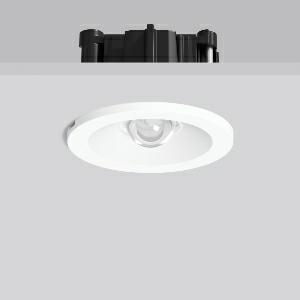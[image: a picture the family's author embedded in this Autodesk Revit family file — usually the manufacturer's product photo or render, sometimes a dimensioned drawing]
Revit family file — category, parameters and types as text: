
# Revit family: turia_l_672411_002_74dd
name_source: partatom
category: Lighting Fixtures
units: mm (PartAtom-declared; Revit-internal decimal feet)

## family parameters
Cut with Voids When Loaded = No
Host = Face
Light Source = No
Part Type = Normal
Room Calculation Point = No
Round Connector Dimension = Use Diameter
Shared = No

## types (1)
- TURIA L (1 x LED Modul 765, 250 lm, 6500)
    Apparent Load = 4 VA
    CIE Flux Codes = 17 57 99 100 100
    Color Rendering = 70
    Color Temperature = 6500
    Default Elevation = 1800 mm
    Description = Series: TURIA L
Round emergency luminaire for escape route lighting. With plastic lenses for area lighting. Suitable for connection to central battery systems. With enclosed separate ceiling mounting ring also suitable for ceiling cut-outs of Ø 68 mm. 
Colour: white
Diameter: 62 mm
Height: 3 mm
Cut-out diameter: 54-68 mm
Recess height: 76-162 mm
Luminaire: recess height: 42 mm
Weight: 230 g
Operating mode: non-maintained power mode
Lamp: LED
Socket: without socket
Colour temperature: 6500K
Colour rendering index (CRI): 70
System power: 3.8 W
Rated luminous flux: 250 lm
Luminous flux, emergency: 250 lm
System power, emergency: 3.8 W
Control gear: Regulated power supply
Protection class: II
Type of protection: IP 20
    Height = 0 mm  [stored 0 ft]
    Lamp = 1 x LED Modul 765
    Lamp Light Flux = 250 lm
    Lamp count = 1
    Length = 62 mm  [stored 0.203412 ft]
    Lifetime = 50000 h
    Luminous efficacy = 66 lm/W
    Manufacturer = RZB
    ModVariant = No
    Model = 672411.002
    Mounting Place = Ceiling
    Mounting Type = Recessed
    Number of Poles = 1
    OnlyDefault = Yes
    Power Factor = 1
    Product Name = TURIA L
    Product group = Recessed ceiling luminaires
    ProductGroupID = 405
    Protection Class = Protection class II
    Protection Degree = IP 20
    RLX_Detail_Level = 1
    RLX_Emergency_Light_Flux = 250 lm
    RLX_Emergency_Type = 3
    RLX_Emergency_Type_DB = Yes
    RlxData = <blob elided: 35125 chars, md5=9275dd96>
    Socket = socket
    Standby Power = 0 W
    System Light Flux = 250 lm
    System Power = 4 W
    Type Comments = Product without accessories
    Type Image = 672412.002.jpg
    URL = http://relux.com
    VarID = ---
    Voltage = 230 V
    Voltage Range = 220-240 V
    Weight = 0.00 kg
    Width = 0 mm  [stored 0 ft]

note: [stored X ft] marks values corroborated as IEEE doubles in the binary element streams (Revit-internal decimal feet)

## geometry (parser evidence)
native form markers: Blend x4, Sweep x12
no freeform markers — native parametric forms only
